# Revit family: 50-151-610_Graa_Fuglerede_simplified
name_source: partatom
category: Generic Models
units: mm (PartAtom-declared; Revit-internal decimal feet)

## family parameters
Always vertical = Yes
Can host rebar = No
Cut with Voids When Loaded = No
Part Type = Normal
Room Calculation Point = No
Round Connector Dimension = Use Diameter
Shared = No
Work Plane-Based = No

## types (1)
- Type 1
    Artnr_Graa-Fuglerede_simplified = 50-151-611
    CheckedDate = -
    CheckedDate_Graa-Fuglerede_simplified = -
    Default Elevation = 0 mm  [stored 0 ft]
    Description = Huske 1 ufo / fuglerede
    Description_Graa-Fuglerede_simplified = Huskestativ 1 Ufo / Fuglerede
    Number = 14750
    Number_Graa-Fuglerede_simplified = 14750
    PartName = Huske 1 ufo / fuglerede
    PartName_Graa-Fuglerede_simplified = Huskestativ 1 Ufo / Fuglerede
    Revision = 0
    Revision_Graa-Fuglerede_simplified = 0

note: [stored X ft] marks values corroborated as IEEE doubles in the binary element streams (Revit-internal decimal feet)

## geometry (parser evidence)
native form markers: Sweep x16
no freeform markers — native parametric forms only
